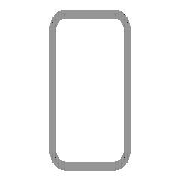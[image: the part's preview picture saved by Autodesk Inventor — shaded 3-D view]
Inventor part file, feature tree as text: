
AUTODESK INVENTOR PART (.ipt)
format: ipt  version: 2025 (Build 290162010, 162A)  size: 134,656 bytes
history: native  units: mm (DEFAULTED — no unit token found)
features: other x4, sketch x1, plane x1
ambient origin geometry x8: Origin, YZ Plane, XZ Plane, XY Plane, X Axis, Y Axis, Z Axis, Center Point
bodies: Solid1 (feature_tree), Body (feature_tree)
feature tree (6):
  parser-record x1  (decoder bookkeeping rows leaked as tree rows — omitted from the tree; the rows remain in map.json)
  other  "Driven Length"
  other  "Start Plane"
  other  "End Plane"
  sketch  "Sketch3"  dims[d3=720.0mm d4=0.0mm d7=6.0mm d9=40.0mm d11=60.0mm d12=3.0mm d13=40.0mm d14=760.0mm d15=20.0mm d16=30.0mm d17=90.0deg d18=720.0mm]
  plane  "Work Plane3"
